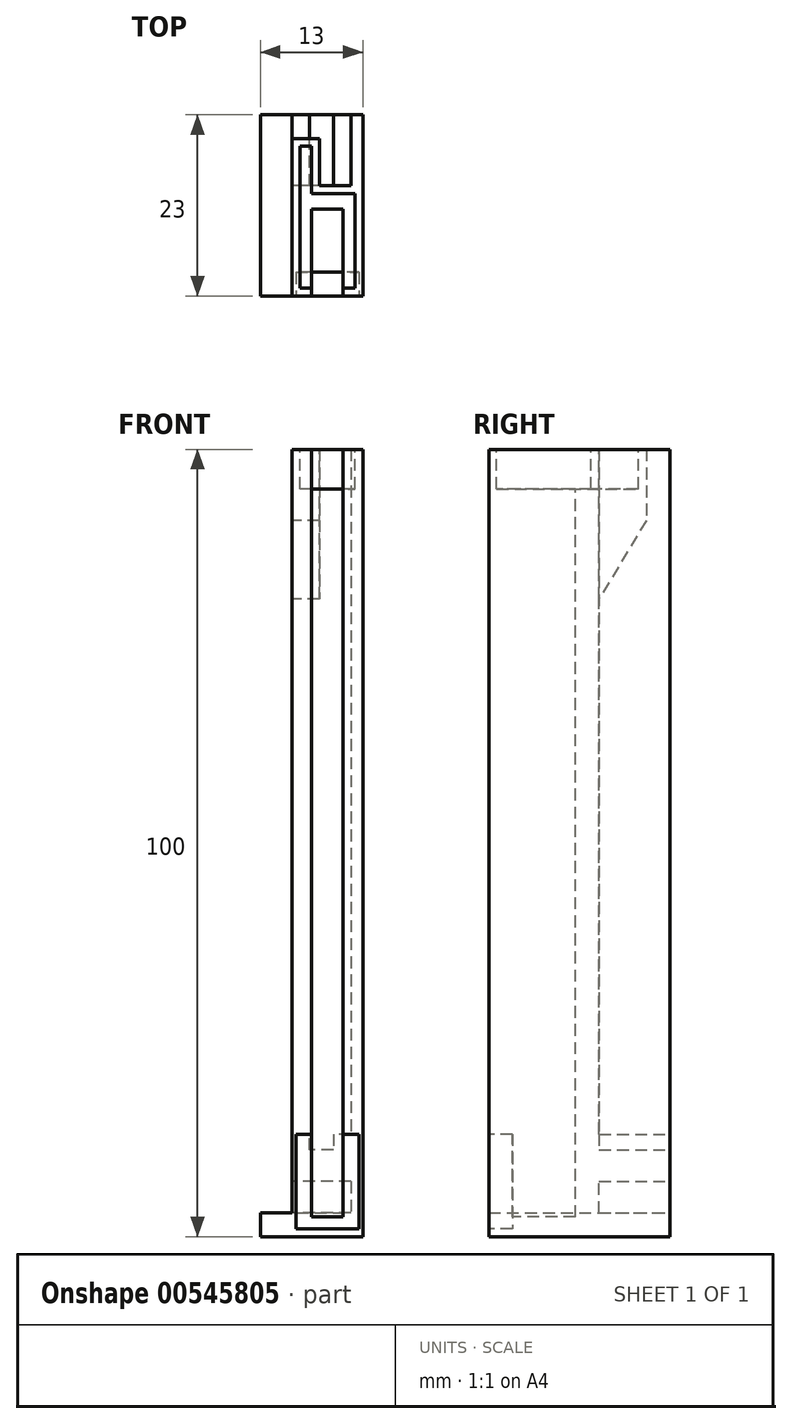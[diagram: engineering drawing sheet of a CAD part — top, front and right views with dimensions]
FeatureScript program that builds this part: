
annotation { "Feature Type Name" : "Feature", "Feature Type Description" : "" }
export const myFeature = defineFeature(function(context is Context, id is Id, definition is map)
    precondition{}
    {
        {
            var Q0;
            Q0=qCreatedBy(makeId("Front.planeOp"),FACE);
            var sketch = newSketch(context, id + "F0", { "sketchPlane" : qUnion([Q0])});
            skLineSegment(sketch, "E0.bottom", {"start": v(0, 100) * mm, "end": v(9, 100) * mm});
            skLineSegment(sketch, "E0.right", {"start": v(9, 100) * mm, "end": v(9, 0) * mm});
            skLineSegment(sketch, "E1", {"start": v(9, 0) * mm, "end": v(-4, 0) * mm});
            skLineSegment(sketch, "E2", {"start": v(-4, 0) * mm, "end": v(-4, 3) * mm});
            skLineSegment(sketch, "E3", {"start": v(-4, 3) * mm, "end": v(0, 3) * mm});
            skLineSegment(sketch, "E4", {"start": v(0, 3) * mm, "end": v(0, 100) * mm});
            skSolve(sketch);
        }
        {
            var Q0;
            Q0=makeQuery(id+"F0.imprint","IMPRINT",FACE,{"disambiguationData":[TD([[makeQuery(id+"F0.imprint","IMPRINT",EDGE,{"derivedFrom":sQuery(id+"F0.wireOp",EDGE,"E0.bottom")}),-1.0]])]});
            extrude(context, id + "F1", {"entities" : qUnion([Q0]), "depth" : 23 * mm, "offsetDistance" : 25 * mm});
        }
        {
            var Q0;
            Q0=makeQuery(id+"F1.opExtrude","CAP_FACE",FACE,{"disambiguationData":[OSD([sQuery(id+"F0.wireOp",EDGE,"E0.bottom"),sQuery(id+"F0.wireOp",EDGE,"E0.right"),sQuery(id+"F0.wireOp",EDGE,"E1"),sQuery(id+"F0.wireOp",EDGE,"E2"),sQuery(id+"F0.wireOp",EDGE,"E3"),sQuery(id+"F0.wireOp",EDGE,"E4")])],"isStart":true});
            var sketch = newSketch(context, id + "F2", { "sketchPlane" : qUnion([Q0])});
            skLineSegment(sketch, "E5", {"start": v(-9, 100) * mm, "end": v(-7.5, 100) * mm});
            skLineSegment(sketch, "E6", {"start": v(-7.5, 100) * mm, "end": v(-7.5, 13) * mm});
            skLineSegment(sketch, "E7", {"start": v(-7.5, 3) * mm, "end": v(4, 3) * mm});
            skLineSegment(sketch, "E8", {"start": v(4, 3) * mm, "end": v(4, 0) * mm});
            skLineSegment(sketch, "E9", {"start": v(4, 0) * mm, "end": v(-9, 0) * mm});
            skLineSegment(sketch, "E10", {"start": v(-9, 0) * mm, "end": v(-9, 100) * mm});
            skLineSegment(sketch, "E11", {"start": v(-7.5, 7) * mm, "end": v(0, 7) * mm});
            skLineSegment(sketch, "E12.trimOffspring", {"start": v(-7.5, 7) * mm, "end": v(-7.5, 3) * mm});
            skLineSegment(sketch, "E13", {"start": v(0, 7) * mm, "end": v(0, 13) * mm});
            skLineSegment(sketch, "E14", {"start": v(-7.5, 13) * mm, "end": v(-5.25, 13) * mm});
            skLineSegment(sketch, "E15", {"start": v(-5.25, 13) * mm, "end": v(-5.25, 11) * mm});
            skLineSegment(sketch, "E16", {"start": v(-5.25, 11) * mm, "end": v(-2.25, 11) * mm});
            skLineSegment(sketch, "E17", {"start": v(-2.25, 11) * mm, "end": v(-2.25, 13) * mm});
            skLineSegment(sketch, "E18", {"start": v(-2.25, 13) * mm, "end": v(0, 13) * mm});
            skSolve(sketch);
        }
        {
            var Q0;
            {var subQ0=sQuery(id+"F2.wireOp",EDGE,"E6");Q0=makeQuery(id+"F2.imprint","IMPRINT",FACE,{"disambiguationData":[TD([[makeQuery(id+"F2.imprint","IMPRINT",EDGE,{"derivedFrom":subQ0}),1.0]])]});}
            var Q1;
            {var subQ4=sQuery(id+"F2.wireOp",EDGE,"E11");Q1=makeQuery(id+"F2.imprint","IMPRINT",FACE,{"disambiguationData":[TD([[makeQuery(id+"F2.imprint","IMPRINT",EDGE,{"derivedFrom":subQ4}),-1.0]])]});}
            extrude(context, id + "F3", {"entities" : qUnion([Q0, Q1]), "operationType" : NewBodyOperationType.REMOVE, "oppositeDirection" : true, "depth" : 9 * mm, "offsetDistance" : 25 * mm});
        }
        {
            var Q0;
            Q0=makeQuery(id+"F1.opExtrude","SWEPT_FACE",FACE,{"disambiguationData":[OSD([sQuery(id+"F0.wireOp",EDGE,"E4")])]});
            var sketch = newSketch(context, id + "F4", { "sketchPlane" : qUnion([Q0])});
            skLineSegment(sketch, "E19", {"start": v(9, 100) * mm, "end": v(3, 100) * mm});
            skLineSegment(sketch, "E20", {"start": v(3, 100) * mm, "end": v(3, 91) * mm});
            skLineSegment(sketch, "E21", {"start": v(3, 91) * mm, "end": v(9, 81) * mm});
            skLineSegment(sketch, "E22", {"start": v(9, 81) * mm, "end": v(9, 100) * mm});
            skSolve(sketch);
        }
        {
            var Q0;
            Q0=makeQuery(id+"F4.imprint","IMPRINT",FACE,{"disambiguationData":[TD([[makeQuery(id+"F4.imprint","IMPRINT",EDGE,{"derivedFrom":sQuery(id+"F4.wireOp",EDGE,"E19")}),1.0]])]});
            extrude(context, id + "F5", {"entities" : qUnion([Q0]), "operationType" : NewBodyOperationType.ADD, "oppositeDirection" : true, "depth" : 3.5 * mm, "offsetDistance" : 25 * mm});
        }
        {
            var Q0;
            Q0=makeQuery(id+"F1.opExtrude","CAP_FACE",FACE,{"disambiguationData":[OSD([sQuery(id+"F0.wireOp",EDGE,"E0.bottom"),sQuery(id+"F0.wireOp",EDGE,"E0.right"),sQuery(id+"F0.wireOp",EDGE,"E1"),sQuery(id+"F0.wireOp",EDGE,"E2"),sQuery(id+"F0.wireOp",EDGE,"E3"),sQuery(id+"F0.wireOp",EDGE,"E4")])],"isStart":false});
            var sketch = newSketch(context, id + "F6", { "sketchPlane" : qUnion([Q0])});
            skLineSegment(sketch, "E23.3", {"start": v(2.5, 97.5) * mm, "end": v(2.5, 2.5) * mm});
            skLineSegment(sketch, "E23.5", {"start": v(6.5, 2.5) * mm, "end": v(6.5, 97.5) * mm});
            skLineSegment(sketch, "E24", {"start": v(6.5, 2.5) * mm, "end": v(2.5, 2.5) * mm});
            skLineSegment(sketch, "E25", {"start": v(2.5, 97.5) * mm, "end": v(2.5, 100) * mm});
            skLineSegment(sketch, "E26", {"start": v(2.5, 100) * mm, "end": v(6.5, 100) * mm});
            skLineSegment(sketch, "E27", {"start": v(6.5, 100) * mm, "end": v(6.5, 97.5) * mm});
            skSolve(sketch);
        }
        {
            var Q0;
            Q0=qSketchRegion(id+"F6",true);
            extrude(context, id + "F7", {"entities" : qUnion([Q0]), "operationType" : NewBodyOperationType.REMOVE, "oppositeDirection" : true, "depth" : 11 * mm, "offsetDistance" : 25 * mm});
        }
        {
            var Q0;
            Q0=makeQuery(id+"F1.opExtrude","CAP_FACE",FACE,{"disambiguationData":[OSD([sQuery(id+"F0.wireOp",EDGE,"E0.bottom"),sQuery(id+"F0.wireOp",EDGE,"E0.right"),sQuery(id+"F0.wireOp",EDGE,"E1"),sQuery(id+"F0.wireOp",EDGE,"E2"),sQuery(id+"F0.wireOp",EDGE,"E3"),sQuery(id+"F0.wireOp",EDGE,"E4")])],"isStart":false});
            var sketch = newSketch(context, id + "F8", { "sketchPlane" : qUnion([Q0])});
            skLineSegment(sketch, "E28", {"start": v(2.5, 13) * mm, "end": v(0.5, 13) * mm});
            skLineSegment(sketch, "E29", {"start": v(0.5, 13) * mm, "end": v(0.5, 1) * mm});
            skLineSegment(sketch, "E30", {"start": v(0.5, 1) * mm, "end": v(8.5, 1) * mm});
            skLineSegment(sketch, "E31", {"start": v(8.5, 1) * mm, "end": v(8.5, 13) * mm});
            skLineSegment(sketch, "E32", {"start": v(8.5, 13) * mm, "end": v(6.5, 13) * mm});
            skLineSegment(sketch, "E33", {"start": v(6.5, 13) * mm, "end": v(6.5, 2.5) * mm});
            skLineSegment(sketch, "E34", {"start": v(6.5, 2.5) * mm, "end": v(2.5, 2.5) * mm});
            skLineSegment(sketch, "E35", {"start": v(2.5, 2.5) * mm, "end": v(2.5, 13) * mm});
            skSolve(sketch);
        }
        {
            var Q0;
            Q0=qSketchRegion(id+"F8",true);
            extrude(context, id + "F9", {"entities" : qUnion([Q0]), "operationType" : NewBodyOperationType.REMOVE, "oppositeDirection" : true, "depth" : 3 * mm, "offsetDistance" : 25 * mm});
        }
        {
            var Q0;
            Q0=makeQuery(id+"F5.boolean.opBoolean","MERGE",FACE,{"derivedFrom":[makeQuery(id+"F1.opExtrude","SWEPT_FACE",FACE,{"disambiguationData":[OSD([sQuery(id+"F0.wireOp",EDGE,"E0.bottom")])]}),makeQuery(id+"F5.opExtrude","SWEPT_FACE",FACE,{"disambiguationData":[OSD([sQuery(id+"F4.wireOp",EDGE,"E19")])]})]});
            var sketch = newSketch(context, id + "F10", { "sketchPlane" : qUnion([Q0])});
            skLineSegment(sketch, "E36", {"start": v(2.5, -22) * mm, "end": v(1, -22) * mm});
            skLineSegment(sketch, "E37", {"start": v(1, -22) * mm, "end": v(1, -4) * mm});
            skLineSegment(sketch, "E38", {"start": v(1, -4) * mm, "end": v(2.5, -4) * mm});
            skLineSegment(sketch, "E39", {"start": v(2.5, -4) * mm, "end": v(2.5, -10) * mm});
            skLineSegment(sketch, "E40", {"start": v(2.5, -10) * mm, "end": v(8, -10) * mm});
            skLineSegment(sketch, "E41", {"start": v(8, -10) * mm, "end": v(8, -22) * mm});
            skLineSegment(sketch, "E42", {"start": v(8, -22) * mm, "end": v(6.5, -22) * mm});
            skLineSegment(sketch, "E43", {"start": v(6.5, -22) * mm, "end": v(6.5, -12) * mm});
            skLineSegment(sketch, "E44", {"start": v(6.5, -12) * mm, "end": v(2.5, -12) * mm});
            skLineSegment(sketch, "E45", {"start": v(2.5, -12) * mm, "end": v(2.5, -22) * mm});
            skSolve(sketch);
        }
        {
            var Q0;
            Q0=qSketchRegion(id+"F10",true);
            extrude(context, id + "F11", {"entities" : qUnion([Q0]), "operationType" : NewBodyOperationType.REMOVE, "oppositeDirection" : true, "depth" : 5 * mm, "offsetDistance" : 25 * mm});
        }
    });
